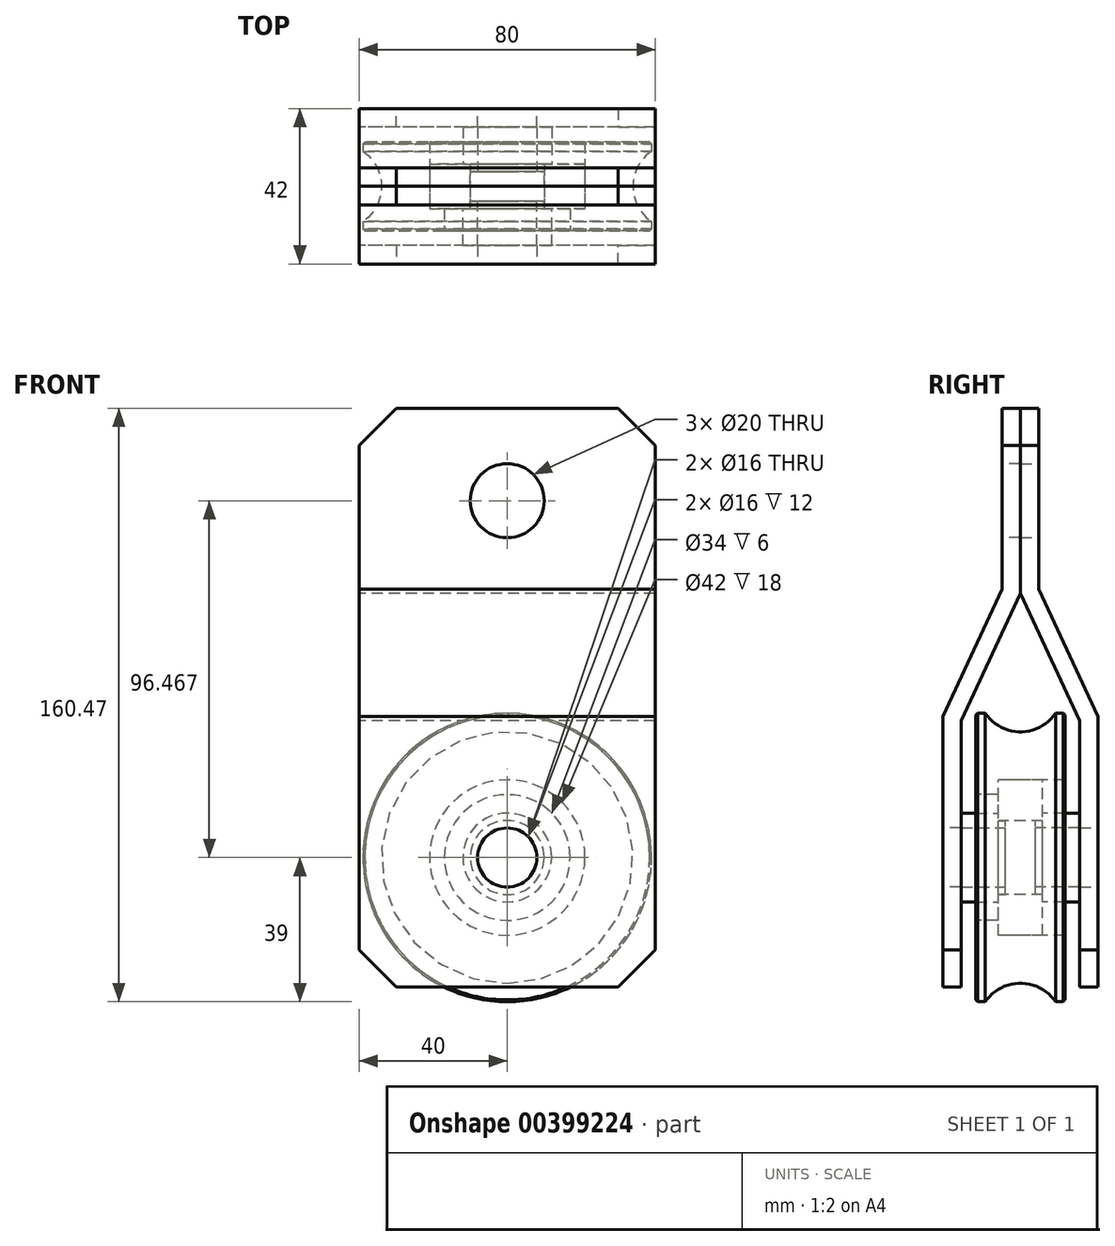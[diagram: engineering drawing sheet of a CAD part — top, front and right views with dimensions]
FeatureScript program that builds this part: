
annotation { "Feature Type Name" : "Feature", "Feature Type Description" : "" }
export const myFeature = defineFeature(function(context is Context, id is Id, definition is map)
    precondition{}
    {
        {
            var Q0;
            Q0=qCreatedBy(makeId("Right.planeOp"),FACE);
            var sketch = newSketch(context, id + "F0", { "sketchPlane" : qUnion([Q0])});
            skLineSegment(sketch, "E0", {"start": v(-24.2, 0) * mm, "end": v(23.6, 0) * mm, "construction": true});
            skLineSegment(sketch, "E1", {"start": v(-12, 17) * mm, "end": v(12, 17) * mm});
            skLineSegment(sketch, "E2", {"start": v(12, 17) * mm, "end": v(12, 39) * mm});
            skLineSegment(sketch, "E3", {"start": v(12, 39) * mm, "end": v(9.5, 39) * mm});
            skLineSegment(sketch, "E4.MirrorCS", {"start": v(-12, 39) * mm, "end": v(-9.5, 39) * mm});
            skLineSegment(sketch, "E5.MirrorCS", {"start": v(-12, 17) * mm, "end": v(-12, 39) * mm});
            skCircle(sketch, "E6", {"center": v(0, 45.53) * mm, "radius": 11.53 * mm});
            skPoint(sketch, "E6.centerSnap0", {"position": v(0, 17) * mm});
            skLineSegment(sketch, "E7", {"start": v(-6, 17) * mm, "end": v(-6, 21) * mm});
            skLineSegment(sketch, "E8", {"start": v(-6, 21) * mm, "end": v(12, 21) * mm});
            skPoint(sketch, "E8.endSnap0", {"position": v(12, 28) * mm});
            skSolve(sketch);
        }
        {
            var Q0;
            {var subQ1=sQuery(id+"F0.wireOp",EDGE,"E3");Q0=makeQuery(id+"F0.imprint","IMPRINT",FACE,{"disambiguationData":[TD([[makeQuery(id+"F0.imprint","IMPRINT",EDGE,{"derivedFrom":subQ1}),1.0]])]});}
            var Q1;
            Q1=sQuery(id+"F0.wireOp",EDGE,"E0");
            revolve(context, id + "F1", {"entities" : qUnion([Q0]), "axis" : qUnion([Q1]), "revolveType" : RevolveType.FULL});
        }
        {
            var Q0;
            Q0=makeQuery(id+"F1.opRevolve","SWEPT_EDGE",EDGE,{"disambiguationData":[OSD([sQuery(id+"F0.wireOp",EDGE,"E2"),sQuery(id+"F0.wireOp",EDGE,"E3")])]});
            var Q1;
            Q1=makeQuery(id+"F1.opRevolve","SWEPT_EDGE",EDGE,{"disambiguationData":[OSD([sQuery(id+"F0.wireOp",EDGE,"E4.MirrorCS"),sQuery(id+"F0.wireOp",EDGE,"E5.MirrorCS")])]});
            chamfer(context, id + "F2", {"entities" : qUnion([Q0, Q1]), "width" : 0.5 * mm, "tangentPropagation" : true});
        }
        {
            var Q0;
            Q0=qCreatedBy(makeId("Right.planeOp"),FACE);
            var sketch = newSketch(context, id + "F3", { "sketchPlane" : qUnion([Q0])});
            skLineSegment(sketch, "E9", {"start": v(-6, 21) * mm, "end": v(6, 21) * mm});
            skLineSegment(sketch, "E10.0.0", {"start": v(-6, 21) * mm, "end": v(-6, 10) * mm, "construction": true});
            skLineSegment(sketch, "E11.top", {"start": v(-6, 10) * mm, "end": v(6, 10) * mm});
            skLineSegment(sketch, "E11.left", {"start": v(-6, 21) * mm, "end": v(-6, 10) * mm});
            skLineSegment(sketch, "E11.right", {"start": v(6, 21) * mm, "end": v(6, 10) * mm});
            skPoint(sketch, "E12.orphan", {"position": v(-6, -21) * mm});
            skLineSegment(sketch, "E13", {"start": v(-29.1, 0) * mm, "end": v(25.21, 0) * mm, "construction": true});
            skSolve(sketch);
        }
        {
            var Q0;
            Q0=qSketchRegion(id+"F3",true);
            var Q1;
            Q1=sQuery(id+"F3.wireOp",EDGE,"E13");
            revolve(context, id + "F4", {"entities" : qUnion([Q0]), "axis" : qUnion([Q1]), "revolveType" : RevolveType.FULL});
        }
        {
            var Q0;
            Q0=qCreatedBy(makeId("Right.planeOp"),FACE);
            var sketch = newSketch(context, id + "F5", { "sketchPlane" : qUnion([Q0])});
            skLineSegment(sketch, "E14", {"start": v(4, 10) * mm, "end": v(6, 10) * mm});
            skLineSegment(sketch, "E15.0.0", {"start": v(6, 12) * mm, "end": v(6, 10) * mm});
            skLineSegment(sketch, "E16", {"start": v(6, 12) * mm, "end": v(16, 12) * mm});
            skLineSegment(sketch, "E17", {"start": v(16, 12) * mm, "end": v(16, 8) * mm});
            skLineSegment(sketch, "E18", {"start": v(16, 8) * mm, "end": v(4, 8) * mm});
            skLineSegment(sketch, "E19", {"start": v(4, 8) * mm, "end": v(4, 10) * mm});
            skPoint(sketch, "E20.orphan", {"position": v(6, 21) * mm});
            skPoint(sketch, "E21.trimOffspring.end.orphan", {"position": v(6, -21) * mm});
            skLineSegment(sketch, "E22", {"start": v(-22.49, 0) * mm, "end": v(21.7, 0) * mm, "construction": true});
            skSolve(sketch);
        }
        {
            var Q0;
            Q0=qSketchRegion(id+"F5",true);
            var Q1;
            Q1=sQuery(id+"F5.wireOp",EDGE,"E22");
            revolve(context, id + "F6", {"entities" : qUnion([Q0]), "axis" : qUnion([Q1]), "revolveType" : RevolveType.FULL});
        }
        {
            var Q0;
            Q0=makeQuery(id+"F6.opRevolve","SWEPT_BODY",BODY,{"disambiguationData":[OSD([sQuery(id+"F5.wireOp",EDGE,"E14"),sQuery(id+"F5.wireOp",EDGE,"E15.0.0"),sQuery(id+"F5.wireOp",EDGE,"E16"),sQuery(id+"F5.wireOp",EDGE,"E17"),sQuery(id+"F5.wireOp",EDGE,"E18"),sQuery(id+"F5.wireOp",EDGE,"E19")])]});
            var Q1;
            Q1=qCreatedBy(makeId("Front.planeOp"),FACE);
            mirror(context, id + "F7", {"entities" : qUnion([Q0]), "mirrorPlane" : qUnion([Q1])});
        }
        {
            var Q0;
            Q0=qCreatedBy(makeId("Right.planeOp"),FACE);
            var sketch = newSketch(context, id + "F8", { "sketchPlane" : qUnion([Q0])});
            skLineSegment(sketch, "E23", {"start": v(16, 37) * mm, "end": v(0, 71.47) * mm});
            skLineSegment(sketch, "E24", {"start": v(0, 71.47) * mm, "end": v(0, 121.47) * mm});
            skLineSegment(sketch, "E25", {"start": v(0, 121.47) * mm, "end": v(5, 121.47) * mm});
            skLineSegment(sketch, "E26", {"start": v(16, 37) * mm, "end": v(16, -35) * mm});
            skLineSegment(sketch, "E27.0", {"start": v(5, 72.57) * mm, "end": v(5, 121.47) * mm});
            skLineSegment(sketch, "E27.1", {"start": v(21, 38.1) * mm, "end": v(5, 72.57) * mm});
            skLineSegment(sketch, "E27.3", {"start": v(21, 38.1) * mm, "end": v(21, -35) * mm});
            skLineSegment(sketch, "E28", {"start": v(16, -35) * mm, "end": v(21, -35) * mm});
            skSolve(sketch);
        }
        {
            var Q0;
            Q0=qSketchRegion(id+"F8",true);
            extrude(context, id + "F9", {"entities" : qUnion([Q0]), "endBound" : BoundingType.SYMMETRIC, "depth" : 80 * mm});
        }
        {
            var Q0;
            Q0=makeQuery(id+"F9.opExtrude","SWEPT_FACE",FACE,{"disambiguationData":[OSD([sQuery(id+"F8.wireOp",EDGE,"E27.3")])]});
            var sketch = newSketch(context, id + "F10", { "sketchPlane" : qUnion([Q0])});
            skCircle(sketch, "E29", {"center": v(0, 0) * mm, "radius": 8 * mm});
            skCircle(sketch, "E30", {"center": v(0, 96.47) * mm, "radius": 10 * mm});
            skPoint(sketch, "E30.centerSnap0", {"position": v(0, 38.1) * mm});
            skSolve(sketch);
        }
        {
            var Q0;
            Q0=makeQuery(id+"F10.imprint","IMPRINT",FACE,{"disambiguationData":[TD([[makeQuery(id+"F10.imprint","IMPRINT",EDGE,{"derivedFrom":sQuery(id+"F10.wireOp",EDGE,"E29")}),1.0]])]});
            var Q1;
            Q1=makeQuery(id+"F10.imprint","IMPRINT",FACE,{"disambiguationData":[TD([[makeQuery(id+"F10.imprint","IMPRINT",EDGE,{"derivedFrom":sQuery(id+"F10.wireOp",EDGE,"E30")}),1.0]])]});
            extrude(context, id + "F11", {"entities" : qUnion([Q0, Q1]), "operationType" : NewBodyOperationType.REMOVE, "endBound" : BoundingType.THROUGH_ALL, "oppositeDirection" : true, "depth" : 25 * mm});
        }
        {
            var Q0;
            Q0=makeQuery(id+"F9.opExtrude","CAP_EDGE",EDGE,{"disambiguationData":[OSD([sQuery(id+"F8.wireOp",EDGE,"E25")])],"isStart":false});
            var Q1;
            Q1=makeQuery(id+"F9.opExtrude","CAP_EDGE",EDGE,{"disambiguationData":[OSD([sQuery(id+"F8.wireOp",EDGE,"E25")])],"isStart":true});
            var Q2;
            Q2=makeQuery(id+"F9.opExtrude","CAP_EDGE",EDGE,{"disambiguationData":[OSD([sQuery(id+"F8.wireOp",EDGE,"E28")])],"isStart":false});
            var Q3;
            Q3=makeQuery(id+"F9.opExtrude","CAP_EDGE",EDGE,{"disambiguationData":[OSD([sQuery(id+"F8.wireOp",EDGE,"E28")])],"isStart":true});
            chamfer(context, id + "F12", {"entities" : qUnion([Q0, Q1, Q2, Q3]), "width" : 10 * mm, "tangentPropagation" : true});
        }
        {
            var Q0;
            Q0=makeQuery(id+"F9.opExtrude","SWEPT_BODY",BODY,{"disambiguationData":[OSD([sQuery(id+"F8.wireOp",EDGE,"E23"),sQuery(id+"F8.wireOp",EDGE,"E24"),sQuery(id+"F8.wireOp",EDGE,"E25"),sQuery(id+"F8.wireOp",EDGE,"E26"),sQuery(id+"F8.wireOp",EDGE,"E27.0"),sQuery(id+"F8.wireOp",EDGE,"E27.1"),sQuery(id+"F8.wireOp",EDGE,"E27.3"),sQuery(id+"F8.wireOp",EDGE,"E28")])]});
            var Q1;
            Q1=qCreatedBy(makeId("Front.planeOp"),FACE);
            mirror(context, id + "F13", {"entities" : qUnion([Q0]), "mirrorPlane" : qUnion([Q1])});
        }
    });
